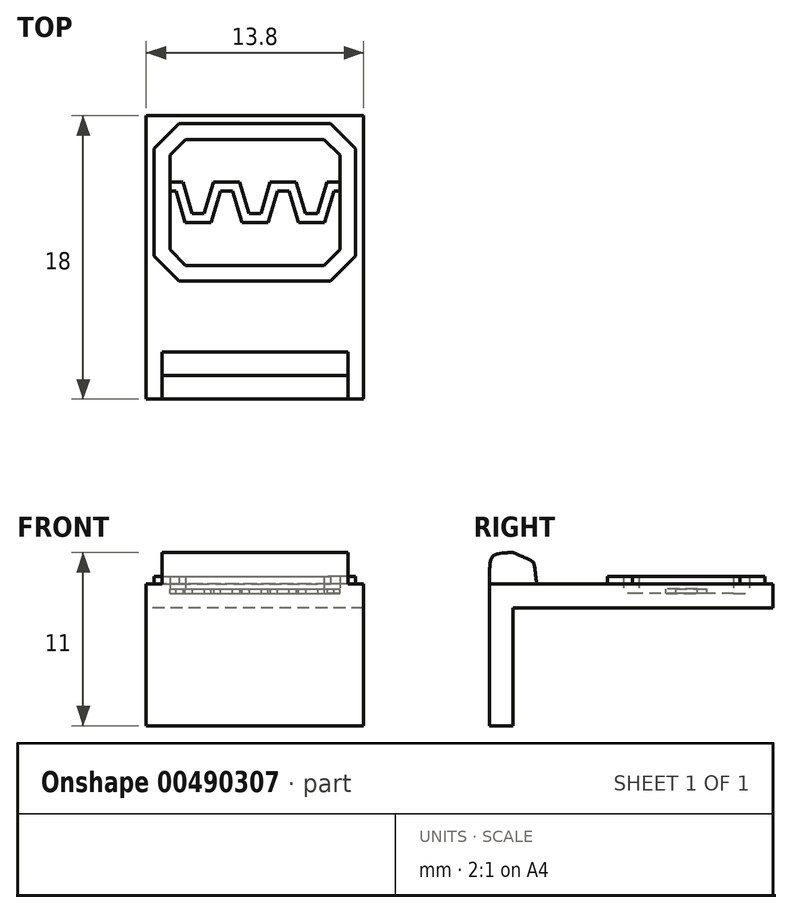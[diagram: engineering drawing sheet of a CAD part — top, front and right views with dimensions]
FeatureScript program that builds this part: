
annotation { "Feature Type Name" : "Feature", "Feature Type Description" : "" }
export const myFeature = defineFeature(function(context is Context, id is Id, definition is map)
    precondition{}
    {
        {
            var Q0;
            Q0=qCreatedBy(makeId("Top.planeOp"),FACE);
            var sketch = newSketch(context, id + "F0", { "sketchPlane" : qUnion([Q0])});
            skLineSegment(sketch, "E0.bottom", {"start": v(0, 0) * mm, "end": v(-13.8, 0) * mm});
            skLineSegment(sketch, "E0.top", {"start": v(0, -18) * mm, "end": v(-13.8, -18) * mm});
            skLineSegment(sketch, "E0.left", {"start": v(0, 0) * mm, "end": v(0, -18) * mm});
            skLineSegment(sketch, "E0.right", {"start": v(-13.8, 0) * mm, "end": v(-13.8, -18) * mm});
            skLineSegment(sketch, "E1", {"start": v(-6.9, 0) * mm, "end": v(-6.9, -18) * mm, "construction": true});
            skLineSegment(sketch, "E2", {"start": v(-11.3, -9.5) * mm, "end": v(-2.5, -9.5) * mm});
            skLineSegment(sketch, "E3", {"start": v(-12.3, -2.5) * mm, "end": v(-12.3, -8.5) * mm});
            skLineSegment(sketch, "E4.MirrorCS", {"start": v(-1.5, -2.5) * mm, "end": v(-1.5, -8.5) * mm});
            skLineSegment(sketch, "E5", {"start": v(-12.3, -2.5) * mm, "end": v(-11.3, -1.5) * mm});
            skLineSegment(sketch, "E6", {"start": v(-12.3, -5.5) * mm, "end": v(-1.5, -5.5) * mm, "construction": true});
            skLineSegment(sketch, "E7.MirrorCS", {"start": v(-1.5, -2.5) * mm, "end": v(-2.5, -1.5) * mm});
            skLineSegment(sketch, "E8.MirrorCS", {"start": v(-1.5, -8.5) * mm, "end": v(-2.5, -9.5) * mm});
            skLineSegment(sketch, "E9.MirrorCS", {"start": v(-12.3, -8.5) * mm, "end": v(-11.3, -9.5) * mm});
            skPoint(sketch, "E10.orphan", {"position": v(-12.3, -1.5) * mm});
            skLineSegment(sketch, "E11.trimOffspring", {"start": v(-11.3, -1.5) * mm, "end": v(-2.5, -1.5) * mm});
            skPoint(sketch, "E12.trimOffspring.start.orphan", {"position": v(-1.5, -1.5) * mm});
            skPoint(sketch, "E13.orphan", {"position": v(-12.3, -9.5) * mm});
            skPoint(sketch, "E14.orphan", {"position": v(-1.5, -9.5) * mm});
            skLineSegment(sketch, "E15.0", {"start": v(-13.3, -2.09) * mm, "end": v(-11.71, -0.5) * mm});
            skLineSegment(sketch, "E15.1", {"start": v(-13.3, -2.09) * mm, "end": v(-13.3, -8.91) * mm});
            skLineSegment(sketch, "E15.2", {"start": v(-11.71, -0.5) * mm, "end": v(-2.09, -0.5) * mm});
            skLineSegment(sketch, "E15.3", {"start": v(-13.3, -8.91) * mm, "end": v(-11.71, -10.5) * mm});
            skLineSegment(sketch, "E15.4", {"start": v(-0.5, -2.09) * mm, "end": v(-2.09, -0.5) * mm});
            skLineSegment(sketch, "E15.5", {"start": v(-0.5, -2.09) * mm, "end": v(-0.5, -8.91) * mm});
            skLineSegment(sketch, "E15.6", {"start": v(-0.5, -8.91) * mm, "end": v(-2.09, -10.5) * mm});
            skLineSegment(sketch, "E15.7", {"start": v(-11.71, -10.5) * mm, "end": v(-2.09, -10.5) * mm});
            skSolve(sketch);
        }
        {
            var Q0;
            Q0=makeQuery(id+"F0.imprint","IMPRINT",FACE,{"disambiguationData":[TD([[makeQuery(id+"F0.imprint","IMPRINT",EDGE,{"derivedFrom":sQuery(id+"F0.wireOp",EDGE,"E0.bottom")}),1.0]])]});
            var Q1;
            Q1=makeQuery(id+"F0.imprint","IMPRINT",FACE,{"disambiguationData":[TD([[makeQuery(id+"F0.imprint","IMPRINT",EDGE,{"derivedFrom":sQuery(id+"F0.wireOp",EDGE,"E2")}),-1.0]])]});
            var Q2;
            Q2=makeQuery(id+"F0.imprint","IMPRINT",FACE,{"disambiguationData":[TD([[makeQuery(id+"F0.imprint","IMPRINT",EDGE,{"derivedFrom":sQuery(id+"F0.wireOp",EDGE,"E2")}),1.0]])]});
            extrude(context, id + "F1", {"entities" : qUnion([Q0, Q1, Q2]), "oppositeDirection" : true, "depth" : 1.5 * mm});
        }
        {
            var Q0;
            Q0=makeQuery(id+"F0.imprint","IMPRINT",FACE,{"disambiguationData":[TD([[makeQuery(id+"F0.imprint","IMPRINT",EDGE,{"derivedFrom":sQuery(id+"F0.wireOp",EDGE,"E2")}),-1.0]])]});
            extrude(context, id + "F2", {"entities" : qUnion([Q0]), "operationType" : NewBodyOperationType.ADD, "depth" : 0.5 * mm});
        }
        {
            var Q0;
            Q0=makeQuery(id+"F0.imprint","IMPRINT",FACE,{"disambiguationData":[TD([[makeQuery(id+"F0.imprint","IMPRINT",EDGE,{"derivedFrom":sQuery(id+"F0.wireOp",EDGE,"E2")}),1.0]])]});
            extrude(context, id + "F3", {"entities" : qUnion([Q0]), "operationType" : NewBodyOperationType.REMOVE, "oppositeDirection" : true, "depth" : 0.6 * mm});
        }
        {
            var Q0;
            Q0=makeQuery(id+"F3.boolean.opBoolean","COPY",FACE,{"derivedFrom":makeQuery(id+"F3.opExtrude","CAP_FACE",FACE,{"disambiguationData":[OSD([sQuery(id+"F0.wireOp",EDGE,"E2"),sQuery(id+"F0.wireOp",EDGE,"E3"),sQuery(id+"F0.wireOp",EDGE,"E4.MirrorCS"),sQuery(id+"F0.wireOp",EDGE,"E5"),sQuery(id+"F0.wireOp",EDGE,"E7.MirrorCS"),sQuery(id+"F0.wireOp",EDGE,"E8.MirrorCS"),sQuery(id+"F0.wireOp",EDGE,"E9.MirrorCS"),sQuery(id+"F0.wireOp",EDGE,"E11.trimOffspring")])],"isStart":false})});
            var sketch = newSketch(context, id + "F4", { "sketchPlane" : qUnion([Q0])});
            skLineSegment(sketch, "E16", {"start": v(-12.3, -5.5) * mm, "end": v(-1.5, -5.5) * mm, "construction": true});
            skLineSegment(sketch, "E17", {"start": v(-6.9, -1.5) * mm, "end": v(-6.9, -9.5) * mm, "construction": true});
            skLineSegment(sketch, "E18", {"start": v(-12.3, -4.5) * mm, "end": v(-1.5, -4.5) * mm, "construction": true});
            skLineSegment(sketch, "E19.MirrorCS", {"start": v(-12.3, -6.5) * mm, "end": v(-1.5, -6.5) * mm, "construction": true});
            skLineSegment(sketch, "E20", {"start": v(-12.3, -4.5) * mm, "end": v(-11.7, -4.5) * mm});
            skLineSegment(sketch, "E21", {"start": v(-11.7, -4.5) * mm, "end": v(-11.1, -6.5) * mm});
            skLineSegment(sketch, "E22", {"start": v(-11.1, -6.5) * mm, "end": v(-9.9, -6.5) * mm});
            skLineSegment(sketch, "E23", {"start": v(-9.9, -6.5) * mm, "end": v(-9.3, -4.5) * mm});
            skLineSegment(sketch, "E24", {"start": v(-9.3, -4.5) * mm, "end": v(-8.1, -4.5) * mm});
            skLineSegment(sketch, "E25", {"start": v(-8.1, -4.5) * mm, "end": v(-7.5, -6.5) * mm});
            skLineSegment(sketch, "E26.1.0.0", {"start": v(-6.3, -6.5) * mm, "end": v(-5.7, -4.5) * mm});
            skLineSegment(sketch, "E26.1.0.1", {"start": v(-5.7, -4.5) * mm, "end": v(-4.5, -4.5) * mm});
            skLineSegment(sketch, "E26.1.0.2", {"start": v(-4.5, -4.5) * mm, "end": v(-3.9, -6.5) * mm});
            skLineSegment(sketch, "E26.1.0.3", {"start": v(-7.5, -6.5) * mm, "end": v(-6.3, -6.5) * mm});
            skLineSegment(sketch, "E26.2.0.0", {"start": v(-2.7, -6.5) * mm, "end": v(-2.1, -4.5) * mm});
            skLineSegment(sketch, "E26.2.0.1", {"start": v(-2.1, -4.5) * mm, "end": v(-1.5, -4.5) * mm});
            skLineSegment(sketch, "E26.2.0.3", {"start": v(-3.9, -6.5) * mm, "end": v(-2.7, -6.5) * mm});
            skLineSegment(sketch, "E26.direction1", {"start": v(-9.9, -6.5) * mm, "end": v(-6.3, -6.5) * mm, "construction": true});
            skPoint(sketch, "E27.orphan", {"position": v(-0.9, -4.5) * mm});
            skSolve(sketch);
        }
        {
            var Q0;
            {var subQ0=sQuery(id+"F0.wireOp",EDGE,"E3");Q0=makeQuery(id+"F3.boolean.opBoolean","MERGE",FACE,{"derivedFrom":[makeQuery(id+"F2.opExtrude","SWEPT_FACE",FACE,{"disambiguationData":[OSD([subQ0])]}),makeQuery(id+"F3.opExtrude","SWEPT_FACE",FACE,{"disambiguationData":[OSD([subQ0])]})]});}
            var sketch = newSketch(context, id + "F5", { "sketchPlane" : qUnion([Q0])});
            skLineSegment(sketch, "E28.bottom", {"start": v(-4.8, -0.6) * mm, "end": v(-4.2, -0.6) * mm});
            skLineSegment(sketch, "E28.top", {"start": v(-4.8, -0.3) * mm, "end": v(-4.2, -0.3) * mm});
            skLineSegment(sketch, "E28.left", {"start": v(-4.8, -0.6) * mm, "end": v(-4.8, -0.3) * mm});
            skLineSegment(sketch, "E28.right", {"start": v(-4.2, -0.6) * mm, "end": v(-4.2, -0.3) * mm});
            skPoint(sketch, "E28.middle", {"position": v(-4.5, -0.45) * mm});
            skPoint(sketch, "E29.0", {"position": v(-4.5, -0.6) * mm});
            skSolve(sketch);
        }
        {
            var Q0;
            Q0=makeQuery(id+"F5.imprint","IMPRINT",FACE,{"disambiguationData":[TD([[makeQuery(id+"F5.imprint","IMPRINT",EDGE,{"derivedFrom":sQuery(id+"F5.wireOp",EDGE,"E28.bottom")}),-1.0]])]});
            var Q1;
            {var subQ0=sQuery(id+"F5.wireOp",EDGE,"E3KQOgvI-YXVx-5YE9-IPWO-YJVoqVIe2fHT");Q1=makeQuery(id+"F5.imprint","IMPRINT",FACE,{"disambiguationData":[TD([[makeQuery(id+"F5.imprint","IMPRINT",EDGE,{"derivedFrom":subQ0}),-1.0]])]});}
            var Q2;
            Q2=sQuery(id+"F4.wireOp",EDGE,"E20");
            var Q3;
            Q3=sQuery(id+"F4.wireOp",EDGE,"E21");
            var Q4;
            Q4=sQuery(id+"F4.wireOp",EDGE,"E22");
            var Q5;
            Q5=sQuery(id+"F4.wireOp",EDGE,"E23");
            var Q6;
            Q6=sQuery(id+"F4.wireOp",EDGE,"E24");
            var Q7;
            Q7=sQuery(id+"F4.wireOp",EDGE,"E25");
            var Q8;
            Q8=sQuery(id+"F4.wireOp",EDGE,"E26.1.0.3");
            var Q9;
            Q9=sQuery(id+"F4.wireOp",EDGE,"E26.1.0.0");
            var Q10;
            Q10=sQuery(id+"F4.wireOp",EDGE,"E26.1.0.1");
            var Q11;
            Q11=sQuery(id+"F4.wireOp",EDGE,"E26.1.0.2");
            var Q12;
            Q12=sQuery(id+"F4.wireOp",EDGE,"E26.2.0.3");
            var Q13;
            Q13=sQuery(id+"F4.wireOp",EDGE,"E26.2.0.0");
            var Q14;
            Q14=sQuery(id+"F4.wireOp",EDGE,"E26.2.0.1");
            sweep(context, id + "F6", {"operationType" : NewBodyOperationType.ADD, "profiles" : qUnion([Q0, Q1]), "path" : qUnion([Q2, Q3, Q4, Q5, Q6, Q7, Q8, Q9, Q10, Q11, Q12, Q13, Q14])});
        }
        {
            var Q0;
            Q0=makeQuery(id+"F1.opExtrude","CAP_FACE",FACE,{"disambiguationData":[OSD([sQuery(id+"F0.wireOp",EDGE,"E0.bottom"),sQuery(id+"F0.wireOp",EDGE,"E0.top"),sQuery(id+"F0.wireOp",EDGE,"E0.left"),sQuery(id+"F0.wireOp",EDGE,"E0.right")])],"isStart":false});
            var sketch = newSketch(context, id + "F7", { "sketchPlane" : qUnion([Q0])});
            skLineSegment(sketch, "E30", {"start": v(0, 16.5) * mm, "end": v(-13.8, 16.5) * mm});
            skSolve(sketch);
        }
        {
            var Q0;
            {var subQ0=sQuery(id+"F7.wireOp",EDGE,"E30");Q0=makeQuery(id+"F7.imprint","IMPRINT",FACE,{"disambiguationData":[TD([[makeQuery(id+"F7.imprint","IMPRINT",EDGE,{"derivedFrom":subQ0}),-1.0]])]});}
            extrude(context, id + "F8", {"entities" : qUnion([Q0]), "operationType" : NewBodyOperationType.ADD, "depth" : 7.5 * mm});
        }
        {
            var Q0;
            {var subQ0=sQuery(id+"F0.wireOp",EDGE,"E0.right");Q0=makeQuery(id+"F8.boolean.opBoolean","MERGE",FACE,{"derivedFrom":[makeQuery(id+"F1.opExtrude","SWEPT_FACE",FACE,{"disambiguationData":[OSD([subQ0])]}),makeQuery(id+"F8.opExtrude","SWEPT_FACE",FACE,{"disambiguationData":[OSD([subQ0])]})]});}
            var sketch = newSketch(context, id + "F9", { "sketchPlane" : qUnion([Q0])});
            skLineSegment(sketch, "E31.bottom", {"start": v(18, 0) * mm, "end": v(15, 0) * mm});
            skLineSegment(sketch, "E31.top", {"start": v(18, 2) * mm, "end": v(15, 2) * mm});
            skLineSegment(sketch, "E31.left", {"start": v(18, 0) * mm, "end": v(18, 2) * mm});
            skLineSegment(sketch, "E31.right", {"start": v(15, 0) * mm, "end": v(15, 2) * mm});
            skSolve(sketch);
        }
        {
            var Q0;
            Q0=makeQuery(id+"F9.imprint","IMPRINT",FACE,{"disambiguationData":[TD([[makeQuery(id+"F9.imprint","IMPRINT",EDGE,{"derivedFrom":sQuery(id+"F9.wireOp",EDGE,"E31.bottom")}),1.0]])]});
            var Q1;
            {var subQ0=sQuery(id+"F0.wireOp",EDGE,"E0.left");Q1=makeQuery(id+"F8.boolean.opBoolean","MERGE",FACE,{"derivedFrom":[makeQuery(id+"F1.opExtrude","SWEPT_FACE",FACE,{"disambiguationData":[OSD([subQ0])]}),makeQuery(id+"F8.opExtrude","SWEPT_FACE",FACE,{"disambiguationData":[OSD([subQ0])]})]});}
            extrude(context, id + "F10", {"entities" : qUnion([Q0]), "operationType" : NewBodyOperationType.ADD, "endBound" : BoundingType.UP_TO_SURFACE, "oppositeDirection" : true, "endBoundEntityFace" : qUnion([Q1]), "depth" : 25 * mm});
        }
        {
            var Q0;
            Q0=makeQuery(id+"F10.opExtrude","SWEPT_EDGE",EDGE,{"disambiguationData":[OSD([sQuery(id+"F9.wireOp",EDGE,"E31.top"),sQuery(id+"F9.wireOp",EDGE,"E31.left")])]});
            fillet(context, id + "F11", {"entities" : qUnion([Q0]), "radius" : 1.5 * mm, "tangentPropagation" : true, "rho" : 0.7, "crossSection" : FilletCrossSection.CONIC, "allowEdgeOverflow" : false});
        }
        {
            var Q0;
            Q0=makeQuery(id+"F10.opExtrude","SWEPT_EDGE",EDGE,{"disambiguationData":[OSD([sQuery(id+"F9.wireOp",EDGE,"E31.top"),sQuery(id+"F9.wireOp",EDGE,"E31.right")])]});
            fillet(context, id + "F12", {"entities" : qUnion([Q0]), "radius" : 2.5 * mm, "tangentPropagation" : true, "rho" : 0.9, "crossSection" : FilletCrossSection.CONIC, "allowEdgeOverflow" : false});
        }
        {
            var Q0;
            {var subQ0=sQuery(id+"F0.wireOp",EDGE,"E0.right");Q0=makeQuery(id+"F10.boolean.opBoolean","MERGE",FACE,{"derivedFrom":[makeQuery(id+"F8.boolean.opBoolean","MERGE",FACE,{"derivedFrom":[makeQuery(id+"F1.opExtrude","SWEPT_FACE",FACE,{"disambiguationData":[OSD([subQ0])]}),makeQuery(id+"F8.opExtrude","SWEPT_FACE",FACE,{"disambiguationData":[OSD([subQ0])]})]}),makeQuery(id+"F10.opExtrude","CAP_FACE",FACE,{"disambiguationData":[OSD([sQuery(id+"F9.wireOp",EDGE,"E31.bottom"),sQuery(id+"F9.wireOp",EDGE,"E31.top"),sQuery(id+"F9.wireOp",EDGE,"E31.left"),sQuery(id+"F9.wireOp",EDGE,"E31.right")])],"isStart":true})]});}
            var sketch = newSketch(context, id + "F13", { "sketchPlane" : qUnion([Q0])});
            skLineSegment(sketch, "E32", {"start": v(15, 0) * mm, "end": v(18, 0) * mm});
            skSolve(sketch);
        }
        {
            var Q0;
            {var subQ0=sQuery(id+"F13.wireOp",EDGE,"E32");Q0=makeQuery(id+"F13.imprint","IMPRINT",FACE,{"disambiguationData":[TD([[makeQuery(id+"F13.imprint","IMPRINT",EDGE,{"derivedFrom":subQ0}),1.0]])]});}
            extrude(context, id + "F14", {"entities" : qUnion([Q0]), "operationType" : NewBodyOperationType.REMOVE, "oppositeDirection" : true, "depth" : 1 * mm});
        }
        {
            var Q0;
            {var subQ0=sQuery(id+"F0.wireOp",EDGE,"E0.left");Q0=makeQuery(id+"F10.boolean.opBoolean","MERGE",FACE,{"derivedFrom":[makeQuery(id+"F8.boolean.opBoolean","MERGE",FACE,{"derivedFrom":[makeQuery(id+"F1.opExtrude","SWEPT_FACE",FACE,{"disambiguationData":[OSD([subQ0])]}),makeQuery(id+"F8.opExtrude","SWEPT_FACE",FACE,{"disambiguationData":[OSD([subQ0])]})]}),makeQuery(id+"F10.opExtrude","CAP_FACE",FACE,{"disambiguationData":[OSD([subQ0])],"isStart":false})]});}
            var sketch = newSketch(context, id + "F15", { "sketchPlane" : qUnion([Q0])});
            skLineSegment(sketch, "E33", {"start": v(-15, 0) * mm, "end": v(-18, 0) * mm});
            skSolve(sketch);
        }
        {
            var Q0;
            {var subQ0=sQuery(id+"F15.wireOp",EDGE,"E33");Q0=makeQuery(id+"F15.imprint","IMPRINT",FACE,{"disambiguationData":[TD([[makeQuery(id+"F15.imprint","IMPRINT",EDGE,{"derivedFrom":subQ0}),-1.0]])]});}
            extrude(context, id + "F16", {"entities" : qUnion([Q0]), "operationType" : NewBodyOperationType.REMOVE, "oppositeDirection" : true, "depth" : 1 * mm});
        }
    });
